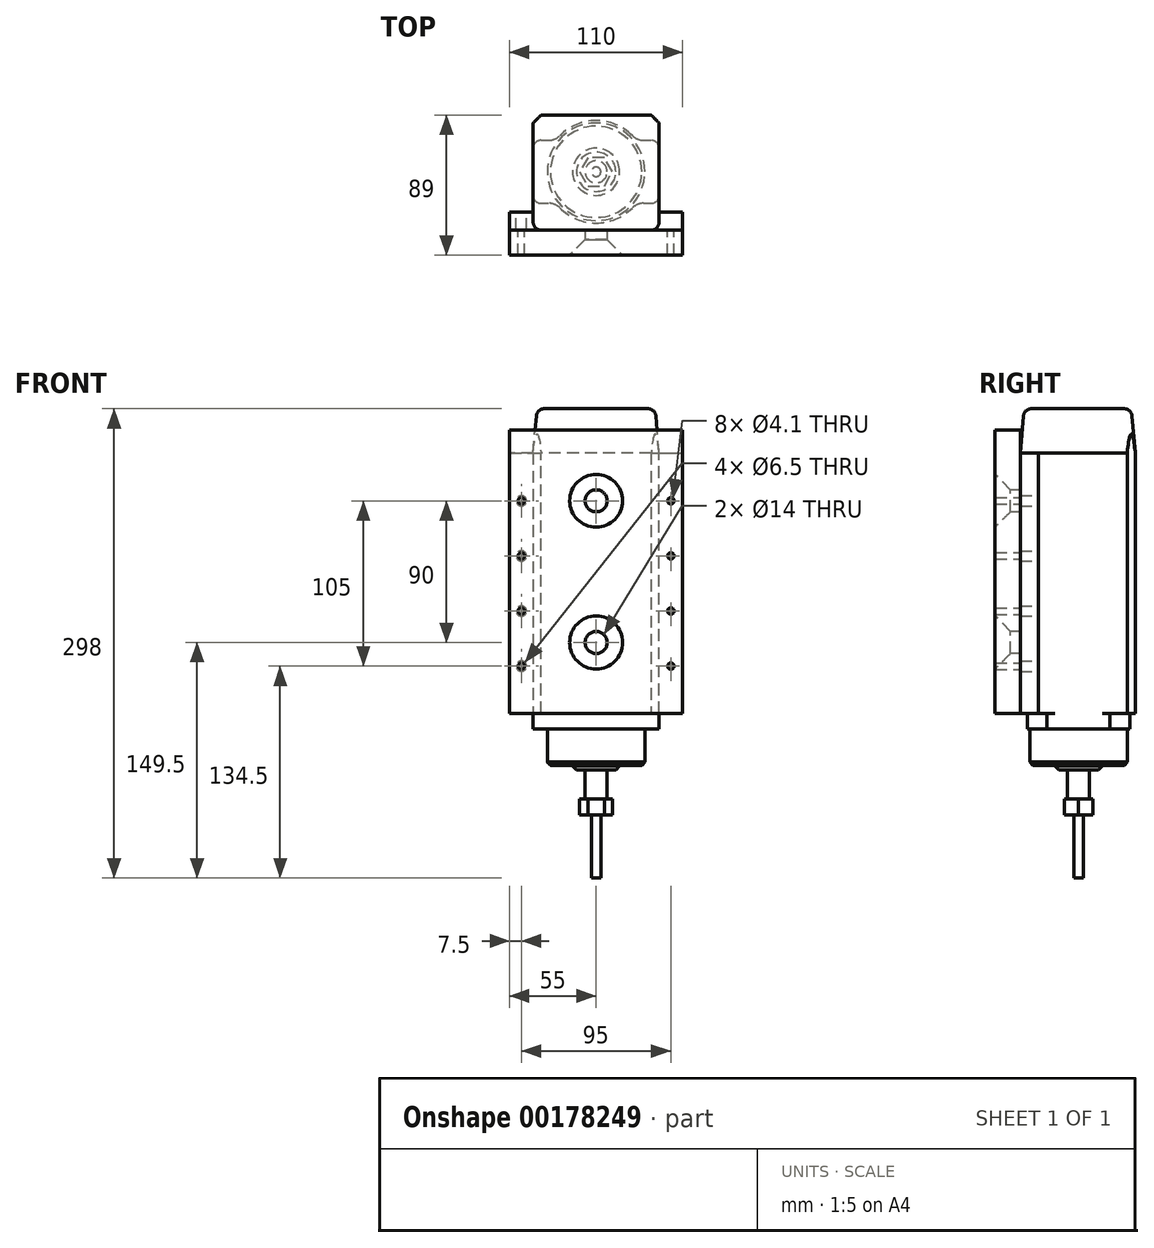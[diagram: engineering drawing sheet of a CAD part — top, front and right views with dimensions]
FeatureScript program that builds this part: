
annotation { "Feature Type Name" : "Feature", "Feature Type Description" : "" }
export const myFeature = defineFeature(function(context is Context, id is Id, definition is map)
    precondition{}
    {
        {
            var Q0;
            Q0=qCreatedBy(makeId("Top.planeOp"),FACE);
            var sketch = newSketch(context, id + "F0", { "sketchPlane" : qUnion([Q0])});
            skLineSegment(sketch, "E0.top", {"start": v(40, 36) * mm, "end": v(-40, 36) * mm});
            skLineSegment(sketch, "E0.left", {"start": v(40, -25.5) * mm, "end": v(40, 36) * mm});
            skLineSegment(sketch, "E0.right", {"start": v(-40, -25.5) * mm, "end": v(-40, 36) * mm});
            skPoint(sketch, "E0.middle", {"position": v(0, 0) * mm});
            skLineSegment(sketch, "E1.top", {"start": v(-40, -25.5) * mm, "end": v(-55, -25.5) * mm});
            skLineSegment(sketch, "E1.right", {"start": v(-55, -37) * mm, "end": v(-55, -25.5) * mm});
            skLineSegment(sketch, "E2.top", {"start": v(40, -25.5) * mm, "end": v(55, -25.5) * mm});
            skLineSegment(sketch, "E2.right", {"start": v(55, -37) * mm, "end": v(55, -25.5) * mm});
            skLineSegment(sketch, "E3", {"start": v(-55, -37) * mm, "end": v(55, -37) * mm});
            skSolve(sketch);
        }
        {
            var Q0;
            Q0=makeQuery(id+"F0.imprint","IMPRINT",FACE,{"disambiguationData":[TD([[makeQuery(id+"F0.imprint","IMPRINT",EDGE,{"derivedFrom":sQuery(id+"F0.wireOp",EDGE,"E0.top")}),1.0]])]});
            extrude(context, id + "F1", {"entities" : qUnion([Q0]), "depth" : 165.5 * mm});
        }
        {
            var Q0;
            Q0=makeQuery(id+"F1.opExtrude","CAP_FACE",FACE,{"disambiguationData":[OSD([sQuery(id+"F0.wireOp",EDGE,"E0.top"),sQuery(id+"F0.wireOp",EDGE,"E0.left"),sQuery(id+"F0.wireOp",EDGE,"E0.right"),sQuery(id+"F0.wireOp",EDGE,"E1.top"),sQuery(id+"F0.wireOp",EDGE,"E1.right"),sQuery(id+"F0.wireOp",EDGE,"E2.top"),sQuery(id+"F0.wireOp",EDGE,"E2.right"),sQuery(id+"F0.wireOp",EDGE,"E3")])],"isStart":false});
            var sketch = newSketch(context, id + "F2", { "sketchPlane" : qUnion([Q0])});
            skLineSegment(sketch, "E4", {"start": v(0, 36) * mm, "end": v(0, -37) * mm, "construction": true});
            skPoint(sketch, "E5", {"position": v(0, 0) * mm});
            skLineSegment(sketch, "E6.bottom", {"start": v(-40, 36) * mm, "end": v(40, 36) * mm});
            skLineSegment(sketch, "E6.top", {"start": v(-40, -37) * mm, "end": v(40, -37) * mm});
            skLineSegment(sketch, "E6.left", {"start": v(-40, 36) * mm, "end": v(-40, -37) * mm});
            skLineSegment(sketch, "E6.right", {"start": v(40, 36) * mm, "end": v(40, -37) * mm});
            skSolve(sketch);
        }
        {
            var Q0;
            Q0=qSketchRegion(id+"F2",true);
            extrude(context, id + "F3", {"entities" : qUnion([Q0]), "operationType" : NewBodyOperationType.ADD, "depth" : 28 * mm, "hasDraft" : true, "draftAngle" : 5 * degree, "draftPullDirection" : true});
        }
        {
            var Q0;
            Q0=makeQuery(id+"F3.opExtrude","SWEPT_EDGE",EDGE,{"disambiguationData":[OSD([sQuery(id+"F0.wireOp",EDGE,"E3"),sQuery(id+"F2.wireOp",EDGE,"E6.top"),sQuery(id+"F2.wireOp",EDGE,"E6.right")])]});
            var Q1;
            Q1=makeQuery(id+"F3.opExtrude","SWEPT_EDGE",EDGE,{"disambiguationData":[OSD([sQuery(id+"F2.wireOp",EDGE,"E6.bottom"),sQuery(id+"F2.wireOp",EDGE,"E6.right")])]});
            var Q2;
            Q2=makeQuery(id+"F3.opExtrude","SWEPT_EDGE",EDGE,{"disambiguationData":[OSD([sQuery(id+"F0.wireOp",EDGE,"E3"),sQuery(id+"F2.wireOp",EDGE,"E6.top"),sQuery(id+"F2.wireOp",EDGE,"E6.left")])]});
            var Q3;
            Q3=makeQuery(id+"F3.opExtrude","SWEPT_EDGE",EDGE,{"disambiguationData":[OSD([sQuery(id+"F2.wireOp",EDGE,"E6.bottom"),sQuery(id+"F2.wireOp",EDGE,"E6.left")])]});
            var Q4;
            Q4=makeQuery(id+"F3.opExtrude","CAP_FACE",FACE,{"disambiguationData":[OSD([sQuery(id+"F2.wireOp",EDGE,"E6.bottom"),sQuery(id+"F2.wireOp",EDGE,"E6.top"),sQuery(id+"F2.wireOp",EDGE,"E6.left"),sQuery(id+"F2.wireOp",EDGE,"E6.right")])],"isStart":false});
            fillet(context, id + "F4", {"entities" : qUnion([Q0, Q1, Q2, Q3, Q4]), "radius" : 5 * mm, "tangentPropagation" : true, "allowEdgeOverflow" : false});
        }
        {
            var Q0;
            Q0=makeQuery(id+"F1.opExtrude","CAP_FACE",FACE,{"disambiguationData":[OSD([sQuery(id+"F0.wireOp",EDGE,"E0.top"),sQuery(id+"F0.wireOp",EDGE,"E0.left"),sQuery(id+"F0.wireOp",EDGE,"E0.right"),sQuery(id+"F0.wireOp",EDGE,"E1.top"),sQuery(id+"F0.wireOp",EDGE,"E1.right"),sQuery(id+"F0.wireOp",EDGE,"E2.top"),sQuery(id+"F0.wireOp",EDGE,"E2.right"),sQuery(id+"F0.wireOp",EDGE,"E3")])],"isStart":true});
            var sketch = newSketch(context, id + "F5", { "sketchPlane" : qUnion([Q0])});
            skArc(sketch, "E7", {"start": v(-23.02, -22.94) * mm, "mid": v(0, -32.5) * mm, "end": v(23.02, -22.94) * mm});
            skLineSegment(sketch, "E8.bottom", {"start": v(-35, -20) * mm, "end": v(-30.1, -20) * mm});
            skLineSegment(sketch, "E8.top", {"start": v(-35, 20) * mm, "end": v(-30.1, 20) * mm});
            skLineSegment(sketch, "E8.left", {"start": v(-40, -15) * mm, "end": v(-40, 15) * mm});
            skLineSegment(sketch, "E8.right", {"start": v(40, -15) * mm, "end": v(40, 15) * mm});
            skArc(sketch, "E9.trimOffspring", {"start": v(23.02, 22.94) * mm, "mid": v(0, 32.5) * mm, "end": v(-23.02, 22.94) * mm});
            skLineSegment(sketch, "E10.trimOffspring", {"start": v(30.1, -20) * mm, "end": v(35, -20) * mm});
            skLineSegment(sketch, "E11.trimOffspring", {"start": v(30.1, 20) * mm, "end": v(35, 20) * mm});
            skPoint(sketch, "E12.visualSharp", {"position": v(-25.62, -20) * mm});
            skArc(sketch, "E12.filletArc", {"start": v(-23.02, -22.94) * mm, "mid": v(-26.27, -20.76) * mm, "end": v(-30.1, -20) * mm});
            skPoint(sketch, "E13.visualSharp", {"position": v(-25.62, 20) * mm});
            skArc(sketch, "E13.filletArc", {"start": v(-30.1, 20) * mm, "mid": v(-26.27, 20.76) * mm, "end": v(-23.02, 22.94) * mm});
            skPoint(sketch, "E14.visualSharp", {"position": v(40, -20) * mm});
            skArc(sketch, "E14.filletArc", {"start": v(35, -20) * mm, "mid": v(38.54, -18.54) * mm, "end": v(40, -15) * mm});
            skPoint(sketch, "E15.visualSharp", {"position": v(40, 20) * mm});
            skArc(sketch, "E15.filletArc", {"start": v(40, 15) * mm, "mid": v(38.54, 18.54) * mm, "end": v(35, 20) * mm});
            skPoint(sketch, "E16.visualSharp", {"position": v(-40, -20) * mm});
            skArc(sketch, "E16.filletArc", {"start": v(-40, -15) * mm, "mid": v(-38.54, -18.54) * mm, "end": v(-35, -20) * mm});
            skPoint(sketch, "E17.visualSharp", {"position": v(-40, 20) * mm});
            skArc(sketch, "E17.filletArc", {"start": v(-35, 20) * mm, "mid": v(-38.54, 18.54) * mm, "end": v(-40, 15) * mm});
            skPoint(sketch, "E18.visualSharp", {"position": v(25.62, 20) * mm});
            skArc(sketch, "E18.filletArc", {"start": v(23.02, 22.94) * mm, "mid": v(26.27, 20.76) * mm, "end": v(30.1, 20) * mm});
            skPoint(sketch, "E19.visualSharp", {"position": v(25.62, -20) * mm});
            skArc(sketch, "E19.filletArc", {"start": v(30.1, -20) * mm, "mid": v(26.27, -20.76) * mm, "end": v(23.02, -22.94) * mm});
            skSolve(sketch);
        }
        {
            var Q0;
            Q0=qSketchRegion(id+"F5",true);
            extrude(context, id + "F6", {"entities" : qUnion([Q0]), "operationType" : NewBodyOperationType.ADD, "depth" : 10 * mm});
        }
        {
            var Q0;
            Q0=makeQuery(id+"F6.opExtrude","CAP_FACE",FACE,{"disambiguationData":[OSD([sQuery(id+"F5.wireOp",EDGE,"E7")])],"isStart":false});
            var sketch = newSketch(context, id + "F7", { "sketchPlane" : qUnion([Q0])});
            skCircle(sketch, "E20", {"center": v(0, 0) * mm, "radius": 31 * mm});
            skSolve(sketch);
        }
        {
            var Q0;
            Q0=qSketchRegion(id+"F7",true);
            extrude(context, id + "F8", {"entities" : qUnion([Q0]), "operationType" : NewBodyOperationType.ADD, "depth" : 23 * mm});
        }
        {
            var Q0;
            Q0=makeQuery(id+"F8.opExtrude","CAP_FACE",FACE,{"disambiguationData":[OSD([sQuery(id+"F7.wireOp",EDGE,"E20")])],"isStart":false});
            var sketch = newSketch(context, id + "F9", { "sketchPlane" : qUnion([Q0])});
            skCircle(sketch, "E21", {"center": v(0, 0) * mm, "radius": 7 * mm});
            skCircle(sketch, "E22", {"center": v(0, 0) * mm, "radius": 15 * mm});
            skSolve(sketch);
        }
        {
            var Q0;
            Q0=makeQuery(id+"F9.imprint","IMPRINT",FACE,{"disambiguationData":[TD([[makeQuery(id+"F9.imprint","IMPRINT",EDGE,{"derivedFrom":sQuery(id+"F9.wireOp",EDGE,"E21")}),1.0]])]});
            extrude(context, id + "F10", {"entities" : qUnion([Q0]), "operationType" : NewBodyOperationType.ADD, "depth" : 31.5 * mm});
        }
        {
            var Q0;
            Q0=makeQuery(id+"F9.imprint","IMPRINT",FACE,{"disambiguationData":[TD([[makeQuery(id+"F9.imprint","IMPRINT",EDGE,{"derivedFrom":sQuery(id+"F9.wireOp",EDGE,"E21")}),-1.0]])]});
            extrude(context, id + "F11", {"entities" : qUnion([Q0]), "operationType" : NewBodyOperationType.ADD, "depth" : 3 * mm});
        }
        {
            var Q0;
            Q0=makeQuery(id+"F10.opExtrude","CAP_FACE",FACE,{"disambiguationData":[OSD([sQuery(id+"F9.wireOp",EDGE,"E21")])],"isStart":false});
            var sketch = newSketch(context, id + "F12", { "sketchPlane" : qUnion([Q0])});
            skCircle(sketch, "E23.cCircle", {"center": v(0, 0) * mm, "radius": 9.03 * mm, "construction": true});
            skLineSegment(sketch, "E23.0", {"start": v(-5.21, 9.03) * mm, "end": v(5.21, 9.03) * mm});
            skLineSegment(sketch, "E23.1", {"start": v(5.21, 9.03) * mm, "end": v(10.43, 0) * mm});
            skLineSegment(sketch, "E23.2", {"start": v(10.43, 0) * mm, "end": v(5.21, -9.03) * mm});
            skLineSegment(sketch, "E23.3", {"start": v(5.21, -9.03) * mm, "end": v(-5.21, -9.03) * mm});
            skLineSegment(sketch, "E23.4", {"start": v(-5.21, -9.03) * mm, "end": v(-10.43, 0) * mm});
            skLineSegment(sketch, "E23.5", {"start": v(-10.43, 0) * mm, "end": v(-5.21, 9.03) * mm});
            skPoint(sketch, "E23.0.midPoint", {"position": v(0, 9.03) * mm});
            skSolve(sketch);
        }
        {
            var Q0;
            Q0=qSketchRegion(id+"F12",true);
            extrude(context, id + "F13", {"entities" : qUnion([Q0]), "operationType" : NewBodyOperationType.ADD, "oppositeDirection" : true, "depth" : 10 * mm});
        }
        {
            var Q0;
            Q0=makeQuery(id+"F13.boolean.opBoolean","MERGE",FACE,{"derivedFrom":[makeQuery(id+"F10.opExtrude","CAP_FACE",FACE,{"disambiguationData":[OSD([sQuery(id+"F9.wireOp",EDGE,"E21")])],"isStart":false}),makeQuery(id+"F13.opExtrude","CAP_FACE",FACE,{"disambiguationData":[OSD([sQuery(id+"F12.wireOp",EDGE,"E23.0"),sQuery(id+"F12.wireOp",EDGE,"E23.1"),sQuery(id+"F12.wireOp",EDGE,"E23.2"),sQuery(id+"F12.wireOp",EDGE,"E23.3"),sQuery(id+"F12.wireOp",EDGE,"E23.4"),sQuery(id+"F12.wireOp",EDGE,"E23.5")])],"isStart":true})]});
            var sketch = newSketch(context, id + "F14", { "sketchPlane" : qUnion([Q0])});
            skCircle(sketch, "E24", {"center": v(0, 0) * mm, "radius": 3 * mm});
            skSolve(sketch);
        }
        {
            var Q0;
            Q0=qSketchRegion(id+"F14",true);
            extrude(context, id + "F15", {"entities" : qUnion([Q0]), "operationType" : NewBodyOperationType.ADD, "depth" : 40 * mm});
        }
        {
            var Q0;
            Q0=makeQuery(id+"F1.opExtrude","SWEPT_EDGE",EDGE,{"disambiguationData":[OSD([sQuery(id+"F0.wireOp",EDGE,"E0.top"),sQuery(id+"F0.wireOp",EDGE,"E0.left")])]});
            var Q1;
            Q1=makeQuery(id+"F1.opExtrude","SWEPT_EDGE",EDGE,{"disambiguationData":[OSD([sQuery(id+"F0.wireOp",EDGE,"E0.top"),sQuery(id+"F0.wireOp",EDGE,"E0.right")])]});
            chamfer(context, id + "F16", {"entities" : qUnion([Q0, Q1]), "width" : 5 * mm, "tangentPropagation" : true});
        }
        {
            var Q0;
            Q0=makeQuery(id+"F1.opExtrude","SWEPT_FACE",FACE,{"disambiguationData":[OSD([sQuery(id+"F0.wireOp",EDGE,"E1.top")])]});
            var sketch = newSketch(context, id + "F17", { "sketchPlane" : qUnion([Q0])});
            skLineSegment(sketch, "E25", {"start": v(47.5, 0) * mm, "end": v(47.5, 165.5) * mm, "construction": true});
            skLineSegment(sketch, "E26", {"start": v(55, 30) * mm, "end": v(40, 30) * mm, "construction": true});
            skLineSegment(sketch, "E27", {"start": v(55, 65) * mm, "end": v(40, 65) * mm, "construction": true});
            skPoint(sketch, "E27.endSnap0", {"position": v(40, 82.75) * mm});
            skLineSegment(sketch, "E28", {"start": v(55, 100) * mm, "end": v(40, 100) * mm, "construction": true});
            skLineSegment(sketch, "E29", {"start": v(55, 135) * mm, "end": v(40, 135) * mm, "construction": true});
            skPoint(sketch, "E30", {"position": v(47.5, 30) * mm});
            skPoint(sketch, "E31", {"position": v(47.5, 65) * mm});
            skPoint(sketch, "E32", {"position": v(47.5, 100) * mm});
            skPoint(sketch, "E33", {"position": v(47.5, 135) * mm});
            skLineSegment(sketch, "E34", {"start": v(0, 8.24) * mm, "end": v(0, 72.92) * mm, "construction": true});
            skSolve(sketch);
        }
        {
            var Q0;
            Q0=sQuery(id+"F17.wireOp",VERTEX,"E30");
            var Q1;
            Q1=sQuery(id+"F17.wireOp",VERTEX,"E31");
            var Q2;
            Q2=sQuery(id+"F17.wireOp",VERTEX,"E32");
            var Q3;
            Q3=sQuery(id+"F17.wireOp",VERTEX,"E33");
            var Q4;
            Q4=makeQuery(id+"F1.opExtrude","SWEPT_BODY",BODY,{"disambiguationData":[OSD([sQuery(id+"F0.wireOp",EDGE,"E0.top"),sQuery(id+"F0.wireOp",EDGE,"E0.left"),sQuery(id+"F0.wireOp",EDGE,"E0.right"),sQuery(id+"F0.wireOp",EDGE,"E1.top"),sQuery(id+"F0.wireOp",EDGE,"E1.right"),sQuery(id+"F0.wireOp",EDGE,"E2.top"),sQuery(id+"F0.wireOp",EDGE,"E2.right"),sQuery(id+"F0.wireOp",EDGE,"E3")])]});
            hole(context, id + "F18", {"style" : HoleStyle.SIMPLE, "endStyle" : HoleEndStyle.THROUGH, "holeDiameter" : 6.5 * mm, "locations" : qUnion([Q0, Q1, Q2, Q3]), "scope" : qUnion([Q4]), "isTappedThrough" : true});
        }
        {
            var Q0;
            Q0=makeQuery(id+"F8.opExtrude","CAP_EDGE",EDGE,{"disambiguationData":[OSD([sQuery(id+"F7.wireOp",EDGE,"E20")])],"isStart":false});
            chamfer(context, id + "F19", {"entities" : qUnion([Q0]), "width" : 2 * mm, "tangentPropagation" : true});
        }
        {
            var Q0;
            Q0=makeQuery(id+"F11.opExtrude","CAP_EDGE",EDGE,{"disambiguationData":[OSD([sQuery(id+"F9.wireOp",EDGE,"E22")])],"isStart":false});
            chamfer(context, id + "F20", {"entities" : qUnion([Q0]), "width" : 2.5 * mm, "tangentPropagation" : true});
        }
        {
            var Q0;
            Q0=makeQuery(id+"F1.opExtrude","SWEPT_FACE",FACE,{"disambiguationData":[OSD([sQuery(id+"F0.wireOp",EDGE,"E3")])]});
            var sketch = newSketch(context, id + "F21", { "sketchPlane" : qUnion([Q0])});
            skLineSegment(sketch, "E35.top", {"start": v(-55, 0) * mm, "end": v(55, 0) * mm});
            skLineSegment(sketch, "E35.right", {"start": v(55, 180) * mm, "end": v(55, 0) * mm});
            skPoint(sketch, "E36", {"position": v(-47.5, 135) * mm});
            skPoint(sketch, "E37", {"position": v(-47.5, 100) * mm});
            skPoint(sketch, "E38", {"position": v(-47.5, 65) * mm});
            skPoint(sketch, "E39", {"position": v(-47.5, 30) * mm});
            skPoint(sketch, "E40", {"position": v(47.5, 135) * mm});
            skPoint(sketch, "E41", {"position": v(47.5, 100) * mm});
            skPoint(sketch, "E42", {"position": v(47.5, 65) * mm});
            skPoint(sketch, "E43", {"position": v(47.5, 30) * mm});
            skLineSegment(sketch, "E44", {"start": v(0, 180) * mm, "end": v(0, 0) * mm, "construction": true});
            skLineSegment(sketch, "E45", {"start": v(-55, 90) * mm, "end": v(55, 90) * mm, "construction": true});
            skPoint(sketch, "E46", {"position": v(0, 135) * mm});
            skPoint(sketch, "E47", {"position": v(0, 45) * mm});
            skLineSegment(sketch, "E48", {"start": v(-55, 180) * mm, "end": v(55, 180) * mm});
            skLineSegment(sketch, "E49", {"start": v(-55, 0) * mm, "end": v(-55, 180) * mm});
            skSolve(sketch);
        }
        {
            var Q0;
            Q0=qSketchRegion(id+"F21",true);
            extrude(context, id + "F22", {"entities" : qUnion([Q0]), "depth" : 16 * mm});
        }
        {
            var Q0;
            Q0=sQuery(id+"F21.wireOp",VERTEX,"E36");
            var Q1;
            Q1=sQuery(id+"F21.wireOp",VERTEX,"E37");
            var Q2;
            Q2=sQuery(id+"F21.wireOp",VERTEX,"E38");
            var Q3;
            Q3=sQuery(id+"F21.wireOp",VERTEX,"E39");
            var Q4;
            Q4=sQuery(id+"F21.wireOp",VERTEX,"E43");
            var Q5;
            Q5=sQuery(id+"F21.wireOp",VERTEX,"E42");
            var Q6;
            Q6=sQuery(id+"F21.wireOp",VERTEX,"E41");
            var Q7;
            Q7=sQuery(id+"F21.wireOp",VERTEX,"E40");
            var Q8;
            Q8=makeQuery(id+"F22.opExtrude","SWEPT_BODY",BODY,{"disambiguationData":[OSD([sQuery(id+"F21.wireOp",EDGE,"E35.top"),sQuery(id+"F21.wireOp",EDGE,"E35.right"),sQuery(id+"F21.wireOp",EDGE,"E48"),sQuery(id+"F21.wireOp",EDGE,"E49")])]});
            hole(context, id + "F23", {"style" : HoleStyle.SIMPLE, "endStyle" : HoleEndStyle.THROUGH, "oppositeDirection" : true, "standardTappedOrClearance" : lookupTablePath({ "standard" : "ISO", "engagement" : "75%", "pitch" : "0.9 mm", "size" : "M5", "type" : "Tapped" }), "standardBlindInLast" : lookupTablePath({ "standard" : "ISO", "engagement" : "75%", "pitch" : "0.9 mm", "size" : "M5", "type" : "Tapped" }), "holeDiameter" : 4.1 * mm, "locations" : qUnion([Q0, Q1, Q2, Q3, Q4, Q5, Q6, Q7]), "scope" : qUnion([Q8]), "isTappedThrough" : true, "showTappedDepth" : true});
        }
        {
            var Q0;
            Q0=makeQuery(id+"F22.opExtrude","CAP_FACE",FACE,{"disambiguationData":[OSD([sQuery(id+"F21.wireOp",EDGE,"E35.top"),sQuery(id+"F21.wireOp",EDGE,"E35.right"),sQuery(id+"F21.wireOp",EDGE,"E48"),sQuery(id+"F21.wireOp",EDGE,"E49")])],"isStart":false});
            var sketch = newSketch(context, id + "F24", { "sketchPlane" : qUnion([Q0])});
            skPoint(sketch, "E50", {"position": v(0, 135) * mm});
            skPoint(sketch, "E51", {"position": v(0, 45) * mm});
            skSolve(sketch);
        }
        {
            var Q0;
            Q0=sQuery(id+"F24.wireOp",VERTEX,"E50");
            var Q1;
            Q1=sQuery(id+"F24.wireOp",VERTEX,"E51");
            var Q2;
            Q2=makeQuery(id+"F22.opExtrude","SWEPT_BODY",BODY,{"disambiguationData":[OSD([sQuery(id+"F21.wireOp",EDGE,"E35.top"),sQuery(id+"F21.wireOp",EDGE,"E35.right"),sQuery(id+"F21.wireOp",EDGE,"E48"),sQuery(id+"F21.wireOp",EDGE,"E49")])]});
            hole(context, id + "F25", {"style" : HoleStyle.C_SINK, "endStyle" : HoleEndStyle.THROUGH, "standardTappedOrClearance" : lookupTablePath({ "standard" : "ISO", "engagement" : "75%", "pitch" : "2 mm", "size" : "M16", "type" : "Tapped" }), "standardBlindInLast" : lookupTablePath({ "standard" : "ISO", "engagement" : "75%", "pitch" : "2 mm", "size" : "M16", "type" : "Tapped" }), "holeDiameter" : 14 * mm, "cSinkDiameter" : 33.6 * mm, "cSinkAngle" : 90 * degree, "locations" : qUnion([Q0, Q1]), "scope" : qUnion([Q2]), "isTappedThrough" : true, "majorDiameter" : 16 * mm, "showTappedDepth" : true});
        }
    });
